# Revit family: NLRS_27_GM_LIB_DR_MR
name_source: partatom
category: Generic Models
units: mm (PartAtom-declared; Revit-internal decimal feet)

## family parameters
Can host rebar = No
Cut with Voids When Loaded = No
Part Type = Normal
Room Calculation Point = No
Round Connector Dimension = Use Diameter
Shared = No

## types (6) — shared parameters
Assembly Code = 27.16
Breedte_Smetplank_1 = 100 mm  [stored 0.328084 ft]
Breedte_Smetplank_2 = 80 mm  [stored 0.262467 ft]
Breedte_Spouw = 350 mm  [stored 1.14829 ft]
Description = Dakranden
Hoogte_Smetplank_1 = 300 mm
Hoogte_Smetplank_2 = 80 mm  [stored 0.262467 ft]
Hoogte_Voorzijde_1 = 200 mm  [stored 0.656168 ft]
Manufacturer = Meilof Riks bv
URL = https://www.meilofriks.nl
false = No
zero-valued in all types: Default Elevation

## per-type parameters (varying)
| type | Breedte_Voorzijde_Totaal | Druppel_1 | Druppel_2 | Model | Type_Dakrand |
| DRA 1 | 400 mm  [stored 1.31234 ft] | Yes | No | DRA | DRA |
| DRVI 1 | 400 mm  [stored 1.31234 ft] | Yes | Yes | DRVI | DRVI |
| DRVVI 1 | 400 mm  [stored 1.31234 ft] | Yes | Yes | DRVVI | DRVVI |
| DRA 2 | 400 mm  [stored 1.31234 ft] | No | No | DRA | DRA |
| DRVI 2 | 450 mm  [stored 1.47638 ft] | Yes | Yes | DRVI | DRVI |
| DRVVI 2 | 400 mm  [stored 1.31234 ft] | No | Yes | DRVVI | DRVVI |

note: [stored X ft] marks values corroborated as IEEE doubles in the binary element streams (Revit-internal decimal feet)

## geometry (parser evidence)
native form markers: Sweep x31
no freeform markers — native parametric forms only
